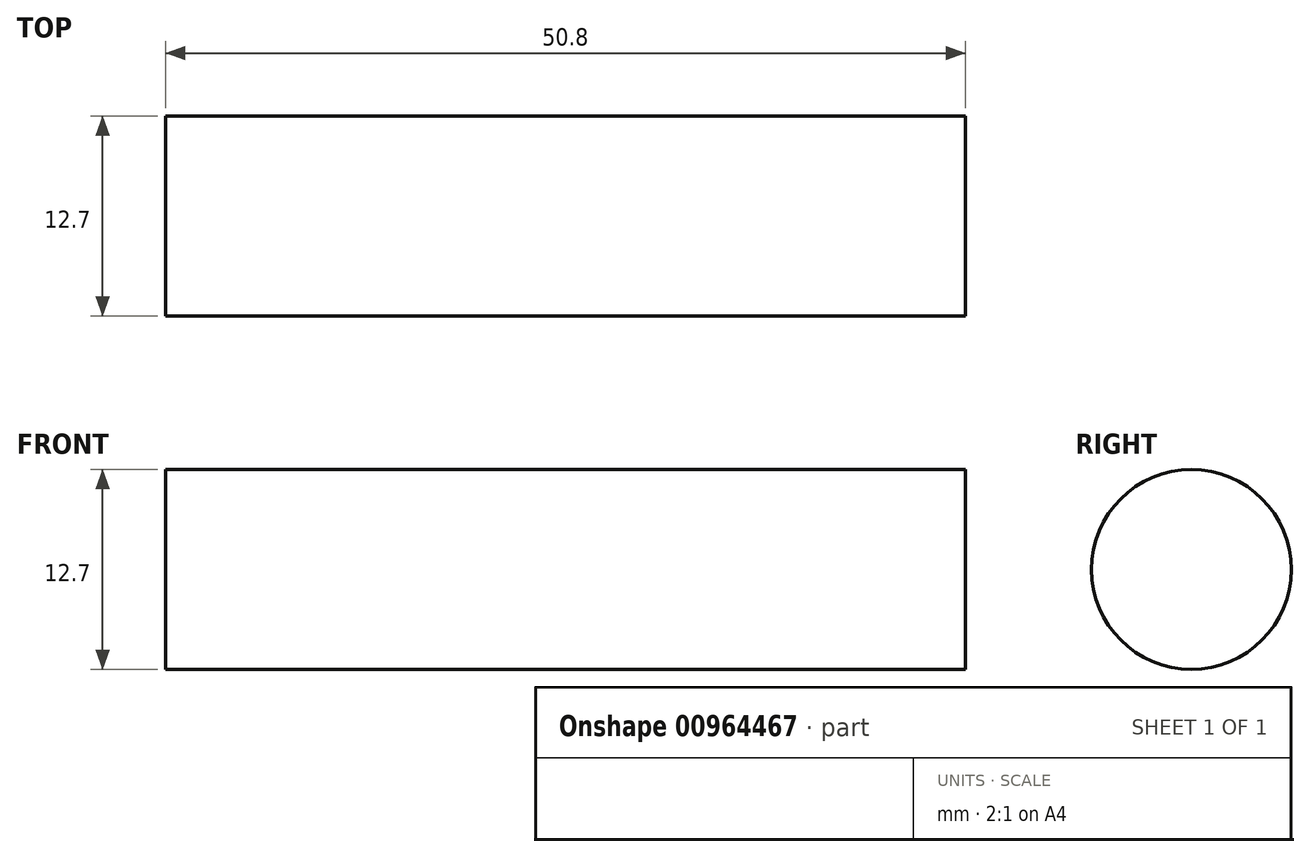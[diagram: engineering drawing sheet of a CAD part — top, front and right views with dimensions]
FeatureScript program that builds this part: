
annotation { "Feature Type Name" : "Feature", "Feature Type Description" : "" }
export const myFeature = defineFeature(function(context is Context, id is Id, definition is map)
    precondition{}
    {
        {
            var Q0;
            Q0=qCreatedBy(makeId("Right.planeOp"),FACE);
            var sketch = newSketch(context, id + "F0", { "sketchPlane" : qUnion([Q0])});
            skCircle(sketch, "E0", {"center": v(0, 0) * mm, "radius": 6.35 * mm});
            skSolve(sketch);
        }
        {
            var Q0;
            Q0 = qSketchRegion(id + "F0", true);
            extrude(context, id + "F1", {"entities" : qUnion([Q0]), "depth" : 50.8 * mm, "offsetDistance" : 25.4 * mm});
        }
    });
